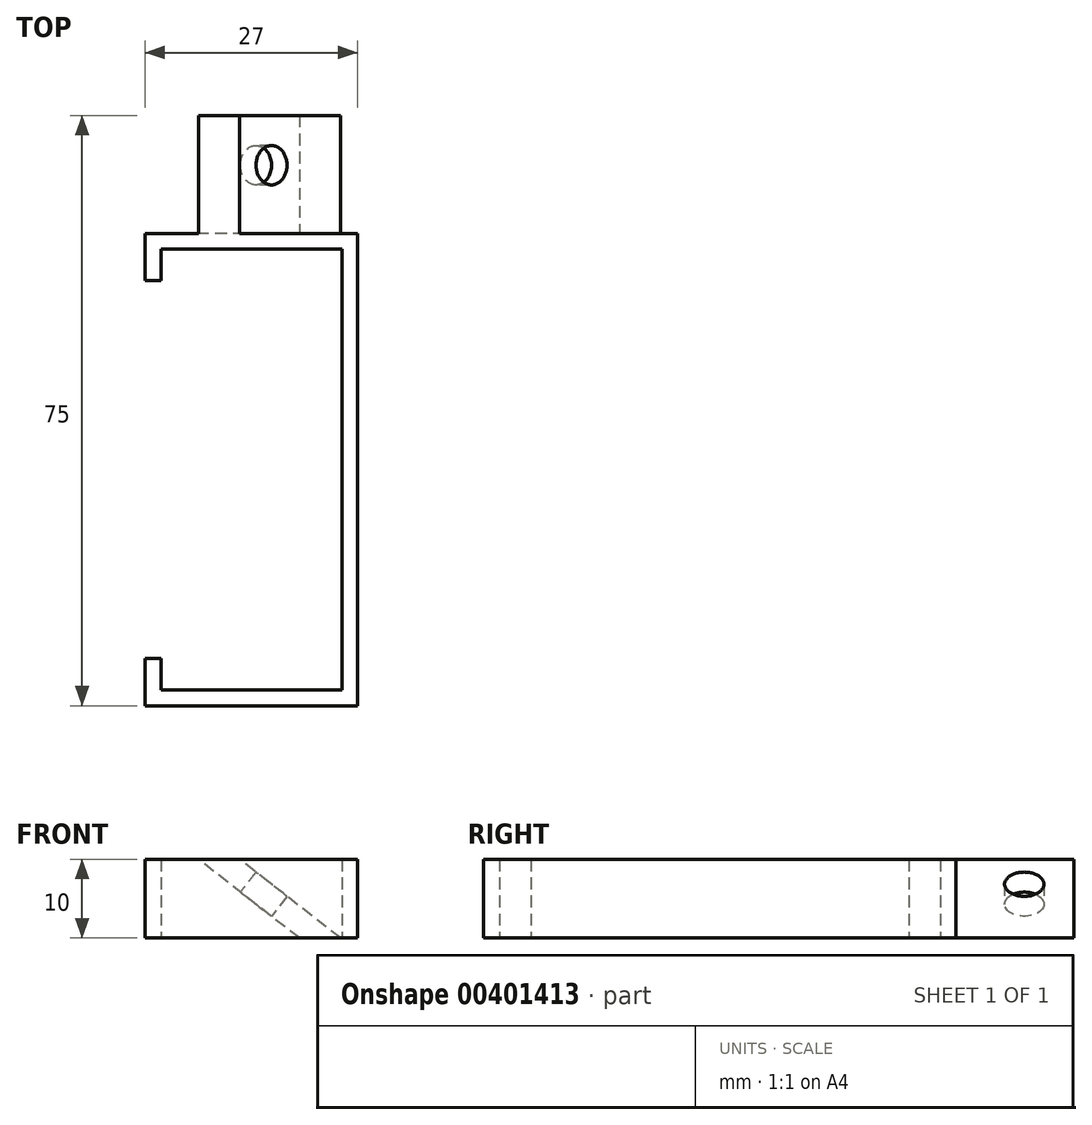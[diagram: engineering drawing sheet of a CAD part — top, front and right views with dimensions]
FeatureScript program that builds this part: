
annotation { "Feature Type Name" : "Feature", "Feature Type Description" : "" }
export const myFeature = defineFeature(function(context is Context, id is Id, definition is map)
    precondition{}
    {
        {
            var Q0;
            Q0=qCreatedBy(makeId("Top.planeOp"),FACE);
            var sketch = newSketch(context, id + "F0", { "sketchPlane" : qUnion([Q0])});
            skLineSegment(sketch, "E0.bottom", {"start": v(13.5, -30) * mm, "end": v(-13.5, -30) * mm});
            skLineSegment(sketch, "E0.top", {"start": v(13.5, 30) * mm, "end": v(-13.5, 30) * mm});
            skLineSegment(sketch, "E0.left", {"start": v(13.5, -30) * mm, "end": v(13.5, 30) * mm});
            skLineSegment(sketch, "E0.right", {"start": v(-13.5, -30) * mm, "end": v(-13.5, -24) * mm});
            skPoint(sketch, "E0.middle", {"position": v(0, 0) * mm});
            skLineSegment(sketch, "E1.bottom", {"start": v(-11.5, -28) * mm, "end": v(11.5, -28) * mm});
            skLineSegment(sketch, "E1.top", {"start": v(-11.5, 28) * mm, "end": v(11.5, 28) * mm});
            skLineSegment(sketch, "E1.left", {"start": v(-13.5, -28) * mm, "end": v(-13.5, -24) * mm});
            skLineSegment(sketch, "E1.right", {"start": v(11.5, -28) * mm, "end": v(11.5, 28) * mm});
            skLineSegment(sketch, "E2.top", {"start": v(-13.5, -24) * mm, "end": v(-11.5, -24) * mm});
            skLineSegment(sketch, "E2.right", {"start": v(-11.5, -28) * mm, "end": v(-11.5, -24) * mm});
            skLineSegment(sketch, "E3.top", {"start": v(-13.5, 24) * mm, "end": v(-11.5, 24) * mm});
            skLineSegment(sketch, "E3.left", {"start": v(-13.5, 28) * mm, "end": v(-13.5, 24) * mm});
            skLineSegment(sketch, "E3.right", {"start": v(-11.5, 28) * mm, "end": v(-11.5, 24) * mm});
            skLineSegment(sketch, "E4.trimOffspring", {"start": v(-13.5, 24) * mm, "end": v(-13.5, 28) * mm});
            skLineSegment(sketch, "E5.trimOffspring", {"start": v(-13.5, 24) * mm, "end": v(-13.5, 30) * mm});
            skSolve(sketch);
        }
        {
            var Q0;
            Q0=makeQuery(id+"F0.imprint","IMPRINT",FACE,{"disambiguationData":[TD([[makeQuery(id+"F0.imprint","IMPRINT",EDGE,{"derivedFrom":sQuery(id+"F0.wireOp",EDGE,"E0.bottom")}),-1.0]])]});
            extrude(context, id + "F1", {"entities" : qUnion([Q0]), "depth" : 10 * mm});
        }
        {
            var Q0;
            Q0=makeQuery(id+"F1.opExtrude","SWEPT_FACE",FACE,{"disambiguationData":[OSD([sQuery(id+"F0.wireOp",EDGE,"E0.top")])]});
            var sketch = newSketch(context, id + "F2", { "sketchPlane" : qUnion([Q0])});
            skLineSegment(sketch, "E6", {"start": v(-6.1, 0) * mm, "end": v(6.73, 10) * mm});
            skLineSegment(sketch, "E7", {"start": v(-11.32, 0) * mm, "end": v(1.5, 10) * mm});
            skSolve(sketch);
        }
        {
            var Q0;
            {var subQ0=sQuery(id+"F2.wireOp",EDGE,"E6");Q0=makeQuery(id+"F2.imprint","IMPRINT",FACE,{"disambiguationData":[TD([[makeQuery(id+"F2.imprint","IMPRINT",EDGE,{"derivedFrom":subQ0}),1.0]])]});}
            extrude(context, id + "F3", {"entities" : qUnion([Q0]), "operationType" : NewBodyOperationType.ADD, "depth" : 15 * mm});
        }
        {
            var Q0;
            Q0=makeQuery(id+"F3.opExtrude","SWEPT_FACE",FACE,{"disambiguationData":[OSD([sQuery(id+"F2.wireOp",EDGE,"E6")])]});
            var sketch = newSketch(context, id + "F4", { "sketchPlane" : qUnion([Q0])});
            skCircle(sketch, "E8", {"center": v(-2.19, -38.68) * mm, "radius": 2.5 * mm});
            skSolve(sketch);
        }
        {
            var Q0;
            Q0=makeQuery(id+"F4.imprint","IMPRINT",FACE,{"disambiguationData":[TD([[makeQuery(id+"F4.imprint","IMPRINT",EDGE,{"derivedFrom":sQuery(id+"F4.wireOp",EDGE,"E8")}),1.0]])]});
            extrude(context, id + "F5", {"entities" : qUnion([Q0]), "operationType" : NewBodyOperationType.REMOVE, "endBound" : BoundingType.THROUGH_ALL, "oppositeDirection" : true, "depth" : 25 * mm});
        }
    });
